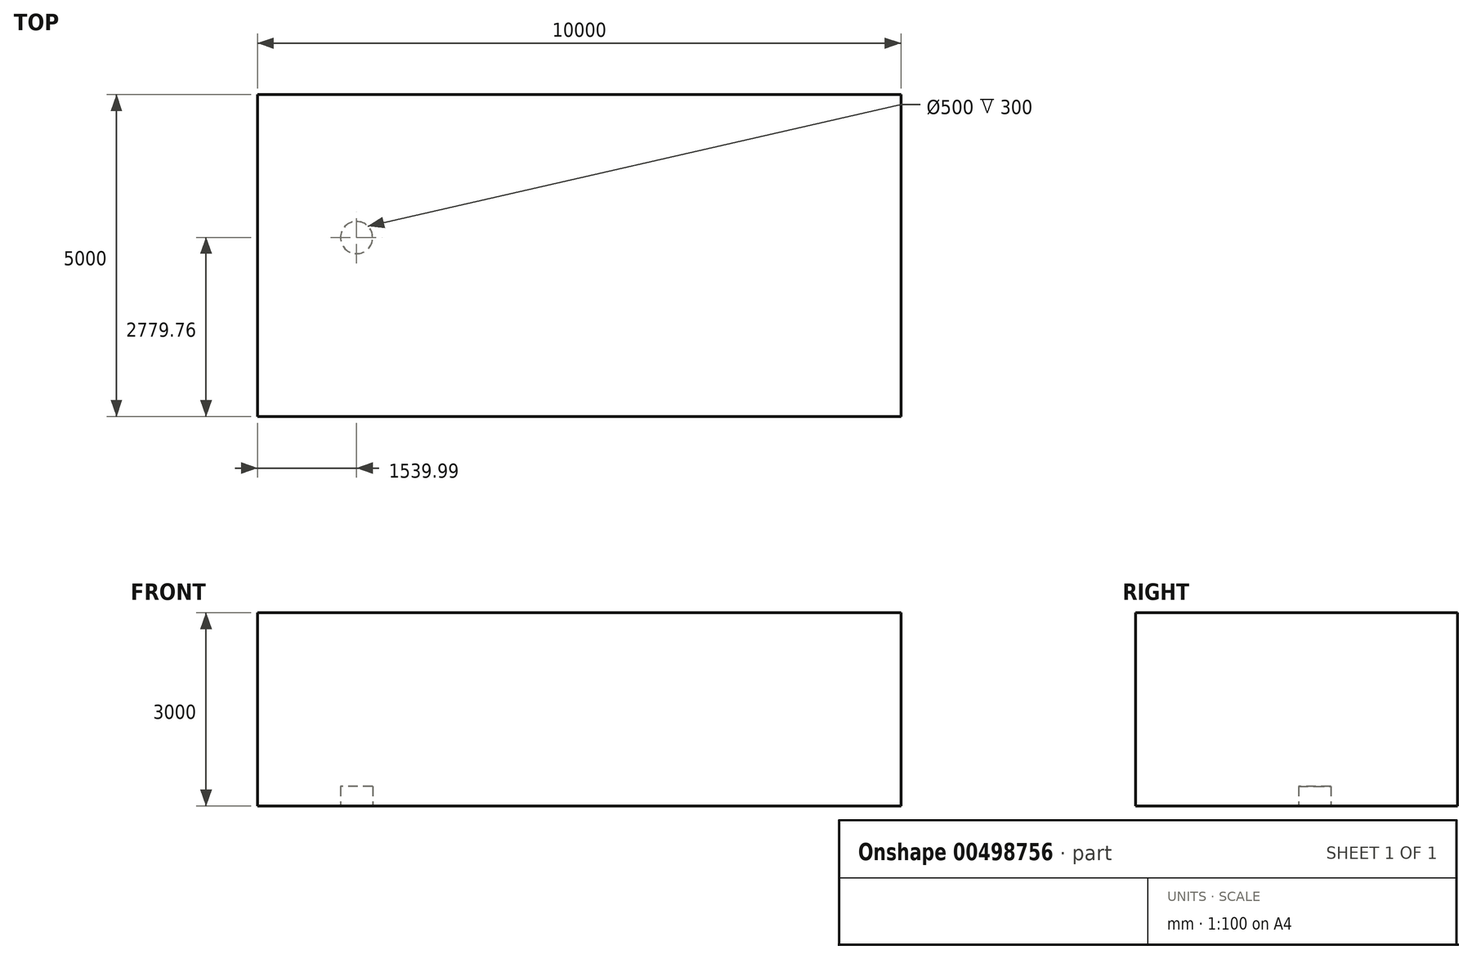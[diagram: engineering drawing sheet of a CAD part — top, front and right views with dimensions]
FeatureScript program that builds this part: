
annotation { "Feature Type Name" : "Feature", "Feature Type Description" : "" }
export const myFeature = defineFeature(function(context is Context, id is Id, definition is map)
    precondition{}
    {
        {
            var Q0;
            Q0=qCreatedBy(makeId("Top.planeOp"),FACE);
            var sketch = newSketch(context, id + "F0", { "sketchPlane" : qUnion([Q0])});
            skLineSegment(sketch, "E0.bottom", {"start": v(-9838.71, 4961.93) * mm, "end": v(161.29, 4961.93) * mm});
            skLineSegment(sketch, "E0.top", {"start": v(-9838.71, -38.07) * mm, "end": v(161.29, -38.07) * mm});
            skLineSegment(sketch, "E0.left", {"start": v(-9838.71, 4961.93) * mm, "end": v(-9838.71, -38.07) * mm});
            skLineSegment(sketch, "E0.right", {"start": v(161.29, 4961.93) * mm, "end": v(161.29, -38.07) * mm});
            skCircle(sketch, "E1", {"center": v(-8298.72, 2741.7) * mm, "radius": 250 * mm});
            skSolve(sketch);
        }
        {
            var Q0;
            Q0=makeQuery(id+"F0.imprint","IMPRINT",FACE,{"disambiguationData":[TD([[makeQuery(id+"F0.imprint","IMPRINT",EDGE,{"derivedFrom":sQuery(id+"F0.wireOp",EDGE,"E0.bottom")}),-1.0]])]});
            var Q1;
            Q1=makeQuery(id+"F0.imprint","IMPRINT",FACE,{"disambiguationData":[TD([[makeQuery(id+"F0.imprint","IMPRINT",EDGE,{"derivedFrom":sQuery(id+"F0.wireOp",EDGE,"E1")}),1.0]])]});
            extrude(context, id + "F1", {"entities" : qUnion([Q0, Q1]), "depth" : 3000 * mm});
        }
        {
            var Q0;
            Q0=makeQuery(id+"F0.imprint","IMPRINT",FACE,{"disambiguationData":[TD([[makeQuery(id+"F0.imprint","IMPRINT",EDGE,{"derivedFrom":sQuery(id+"F0.wireOp",EDGE,"E1")}),1.0]])]});
            extrude(context, id + "F2", {"entities" : qUnion([Q0]), "operationType" : NewBodyOperationType.REMOVE, "depth" : 300 * mm});
        }
    });
